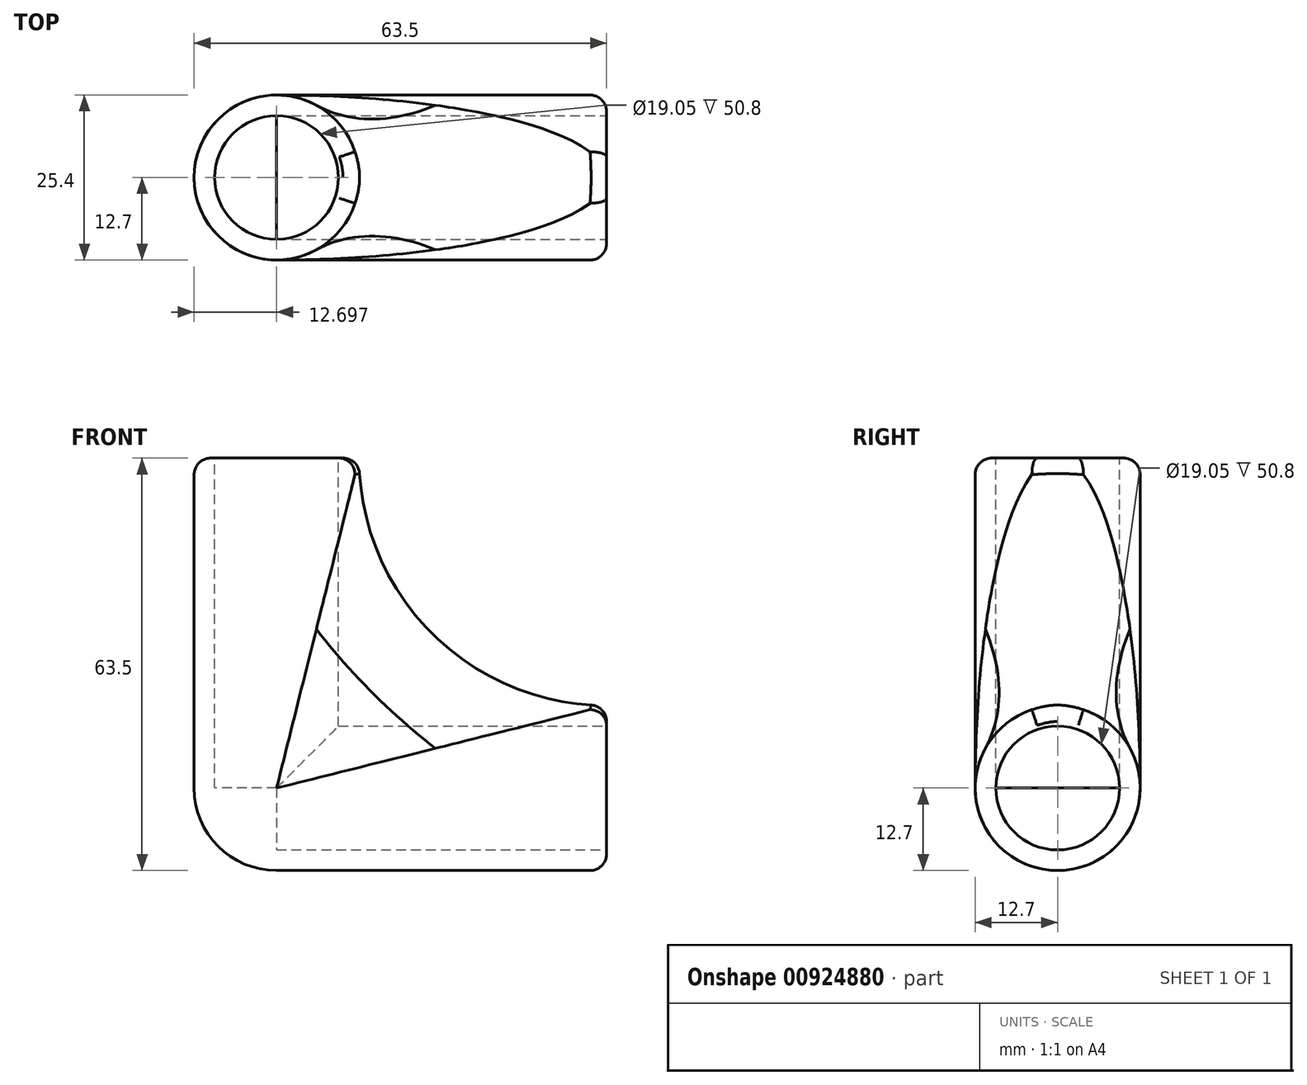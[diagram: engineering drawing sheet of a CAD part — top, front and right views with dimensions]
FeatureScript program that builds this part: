
annotation { "Feature Type Name" : "Feature", "Feature Type Description" : "" }
export const myFeature = defineFeature(function(context is Context, id is Id, definition is map)
    precondition{}
    {
        {
            var Q0;
            Q0=qCreatedBy(makeId("Front.planeOp"),FACE);
            var sketch = newSketch(context, id + "F0", { "sketchPlane" : qUnion([Q0])});
            skLineSegment(sketch, "E0.bottom", {"start": v(-30.34, 11.67) * mm, "end": v(33.16, 11.67) * mm});
            skLineSegment(sketch, "E0.top", {"start": v(-30.34, -13.73) * mm, "end": v(33.16, -13.73) * mm});
            skLineSegment(sketch, "E0.left", {"start": v(-30.34, 11.67) * mm, "end": v(-30.34, -13.73) * mm});
            skLineSegment(sketch, "E0.right", {"start": v(33.16, 11.67) * mm, "end": v(33.16, -13.73) * mm});
            skLineSegment(sketch, "E1.bottom", {"start": v(-30.34, 11.67) * mm, "end": v(-4.94, 11.67) * mm});
            skLineSegment(sketch, "E1.top", {"start": v(-30.34, 49.77) * mm, "end": v(-4.94, 49.77) * mm});
            skLineSegment(sketch, "E1.left", {"start": v(-30.34, 11.67) * mm, "end": v(-30.34, 49.77) * mm});
            skLineSegment(sketch, "E1.right", {"start": v(-4.94, 11.67) * mm, "end": v(-4.94, 49.77) * mm});
            skSolve(sketch);
        }
        {
            var Q0;
            Q0 = qSketchRegion(id + "F0", true);
            extrude(context, id + "F1", {"entities" : qUnion([Q0]), "depth" : 25.4 * mm, "offsetDistance" : 25.4 * mm});
        }
        {
            var Q0;
            Q0=makeQuery(id+"F1.opExtrude","CAP_EDGE",EDGE,{"disambiguationData":[OSD([sQuery(id+"F0.wireOp",EDGE,"E0.left"),sQuery(id+"F0.wireOp",EDGE,"E1.left")])],"isStart":false});
            var Q1;
            Q1=makeQuery(id+"F1.opExtrude","CAP_EDGE",EDGE,{"disambiguationData":[OSD([sQuery(id+"F0.wireOp",EDGE,"E1.right")])],"isStart":false});
            var Q2;
            Q2=makeQuery(id+"F1.opExtrude","CAP_EDGE",EDGE,{"disambiguationData":[OSD([sQuery(id+"F0.wireOp",EDGE,"E1.right")])],"isStart":true});
            var Q3;
            Q3=makeQuery(id+"F1.opExtrude","CAP_EDGE",EDGE,{"disambiguationData":[OSD([sQuery(id+"F0.wireOp",EDGE,"E0.bottom")])],"isStart":false});
            var Q4;
            Q4=makeQuery(id+"F1.opExtrude","CAP_EDGE",EDGE,{"disambiguationData":[OSD([sQuery(id+"F0.wireOp",EDGE,"E0.top")])],"isStart":false});
            var Q5;
            Q5=makeQuery(id+"F1.opExtrude","SWEPT_EDGE",EDGE,{"disambiguationData":[OSD([sQuery(id+"F0.wireOp",EDGE,"E0.top"),sQuery(id+"F0.wireOp",EDGE,"E0.left")])]});
            var Q6;
            Q6=makeQuery(id+"F1.opExtrude","CAP_EDGE",EDGE,{"disambiguationData":[OSD([sQuery(id+"F0.wireOp",EDGE,"E0.left"),sQuery(id+"F0.wireOp",EDGE,"E1.left")])],"isStart":true});
            var Q7;
            Q7=makeQuery(id+"F1.opExtrude","CAP_EDGE",EDGE,{"disambiguationData":[OSD([sQuery(id+"F0.wireOp",EDGE,"E0.bottom")])],"isStart":true});
            var Q8;
            Q8=makeQuery(id+"F1.opExtrude","CAP_EDGE",EDGE,{"disambiguationData":[OSD([sQuery(id+"F0.wireOp",EDGE,"E0.top")])],"isStart":true});
            fillet(context, id + "F2", {"entities" : qUnion([Q0, Q1, Q2, Q3, Q4, Q5, Q6, Q7, Q8]), "radius" : 12.7 * mm, "tangentPropagation" : true, "allowEdgeOverflow" : false});
        }
        {
            var Q0;
            Q0=makeQuery(id+"F1.opExtrude","SWEPT_FACE",FACE,{"disambiguationData":[OSD([sQuery(id+"F0.wireOp",EDGE,"E0.right")])]});
            var sketch = newSketch(context, id + "F3", { "sketchPlane" : qUnion([Q0])});
            skCircle(sketch, "E2", {"center": v(-12.7, -1.03) * mm, "radius": 9.53 * mm});
            skSolve(sketch);
        }
        {
            var Q0;
            Q0=makeQuery(id+"F2.opFillet","BLEND_EDGE",EDGE,{"blendedFrom":[makeQuery(id+"F1.opExtrude","CAP_EDGE",EDGE,{"disambiguationData":[OSD([sQuery(id+"F0.wireOp",EDGE,"E0.bottom")])],"isStart":true}),makeQuery(id+"F1.opExtrude","CAP_EDGE",EDGE,{"disambiguationData":[OSD([sQuery(id+"F0.wireOp",EDGE,"E1.right")])],"isStart":true})],"blendedInto":[]});
            fillet(context, id + "F4", {"entities" : qUnion([Q0]), "radius" : 38.1 * mm, "tangentPropagation" : true, "allowEdgeOverflow" : false});
        }
        {
            var Q0;
            Q0=makeQuery(id+"F3.imprint","IMPRINT",FACE,{"disambiguationData":[TD([[makeQuery(id+"F3.imprint","IMPRINT",EDGE,{"derivedFrom":sQuery(id+"F3.wireOp",EDGE,"E2")}),1.0]])]});
            extrude(context, id + "F5", {"entities" : qUnion([Q0]), "operationType" : NewBodyOperationType.REMOVE, "oppositeDirection" : true, "depth" : 50.8 * mm, "offsetDistance" : 25.4 * mm});
        }
        {
            var Q0;
            Q0=makeQuery(id+"F1.opExtrude","SWEPT_FACE",FACE,{"disambiguationData":[OSD([sQuery(id+"F0.wireOp",EDGE,"E1.top")])]});
            var sketch = newSketch(context, id + "F6", { "sketchPlane" : qUnion([Q0])});
            skCircle(sketch, "E3", {"center": v(-17.64, -12.7) * mm, "radius": 9.53 * mm});
            skSolve(sketch);
        }
        {
            var Q0;
            Q0=makeQuery(id+"F6.imprint","IMPRINT",FACE,{"disambiguationData":[TD([[makeQuery(id+"F6.imprint","IMPRINT",EDGE,{"derivedFrom":sQuery(id+"F6.wireOp",EDGE,"E3")}),1.0]])]});
            extrude(context, id + "F7", {"entities" : qUnion([Q0]), "operationType" : NewBodyOperationType.REMOVE, "oppositeDirection" : true, "depth" : 50.8 * mm, "offsetDistance" : 25.4 * mm});
        }
        {
            var Q0;
            Q0=makeQuery(id+"F2.opFillet","BLEND_EDGE",EDGE,{"blendedFrom":[makeQuery(id+"F1.opExtrude","CAP_EDGE",EDGE,{"disambiguationData":[OSD([sQuery(id+"F0.wireOp",EDGE,"E0.bottom")])],"isStart":true}),makeQuery(id+"F1.opExtrude","SWEPT_FACE",FACE,{"disambiguationData":[OSD([sQuery(id+"F0.wireOp",EDGE,"E0.right")])]})],"blendedInto":[makeQuery(id+"F1.opExtrude","SWEPT_FACE",FACE,{"disambiguationData":[OSD([sQuery(id+"F0.wireOp",EDGE,"E0.right")])]})]});
            var Q1;
            Q1=makeQuery(id+"F2.opFillet","BLEND_EDGE",EDGE,{"blendedFrom":[makeQuery(id+"F1.opExtrude","CAP_EDGE",EDGE,{"disambiguationData":[OSD([sQuery(id+"F0.wireOp",EDGE,"E0.left"),sQuery(id+"F0.wireOp",EDGE,"E1.left")])],"isStart":true}),makeQuery(id+"F1.opExtrude","SWEPT_FACE",FACE,{"disambiguationData":[OSD([sQuery(id+"F0.wireOp",EDGE,"E1.top")])]})],"blendedInto":[makeQuery(id+"F1.opExtrude","SWEPT_FACE",FACE,{"disambiguationData":[OSD([sQuery(id+"F0.wireOp",EDGE,"E1.top")])]})]});
            fillet(context, id + "F8", {"entities" : qUnion([Q0, Q1]), "radius" : 2.54 * mm, "tangentPropagation" : true, "allowEdgeOverflow" : false});
        }
    });
